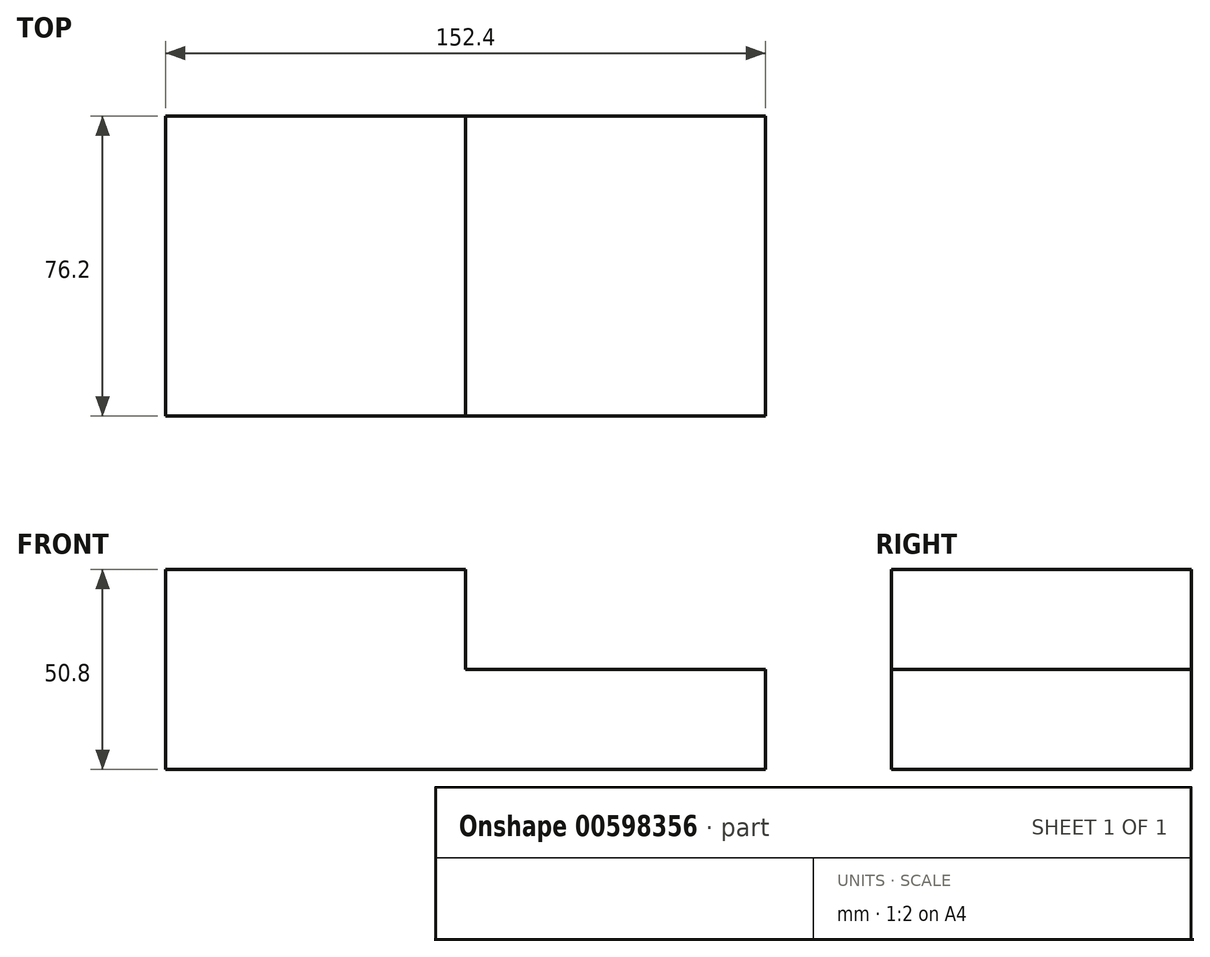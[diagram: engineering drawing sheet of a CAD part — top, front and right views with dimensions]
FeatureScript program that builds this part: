
annotation { "Feature Type Name" : "Feature", "Feature Type Description" : "" }
export const myFeature = defineFeature(function(context is Context, id is Id, definition is map)
    precondition{}
    {
        {
            var Q0;
            Q0=qCreatedBy(makeId("Front.planeOp"),FACE);
            var sketch = newSketch(context, id + "F0", { "sketchPlane" : qUnion([Q0])});
            skLineSegment(sketch, "E0", {"start": v(0, 0) * mm, "end": v(0, 50.8) * mm});
            skLineSegment(sketch, "E1", {"start": v(0, 50.8) * mm, "end": v(76.2, 50.8) * mm});
            skLineSegment(sketch, "E2", {"start": v(76.2, 50.8) * mm, "end": v(76.2, 25.4) * mm});
            skLineSegment(sketch, "E3", {"start": v(0, 0) * mm, "end": v(152.4, 0) * mm});
            skLineSegment(sketch, "E4", {"start": v(76.2, 25.4) * mm, "end": v(152.4, 25.4) * mm});
            skLineSegment(sketch, "E5", {"start": v(152.4, 25.4) * mm, "end": v(152.4, 0) * mm});
            skSolve(sketch);
        }
        {
            var Q0;
            Q0 = qSketchRegion(id + "F0", true);
            extrude(context, id + "F1", {"entities" : qUnion([Q0]), "depth" : 76.2 * mm, "offsetDistance" : 25.4 * mm});
        }
        {
            var Q0;
            Q0 = qSketchRegion(id + "F0", true);
            extrude(context, id + "F2", {"entities" : qUnion([Q0]), "operationType" : NewBodyOperationType.ADD, "depth" : 76.2 * mm, "offsetDistance" : 25.4 * mm});
        }
    });
